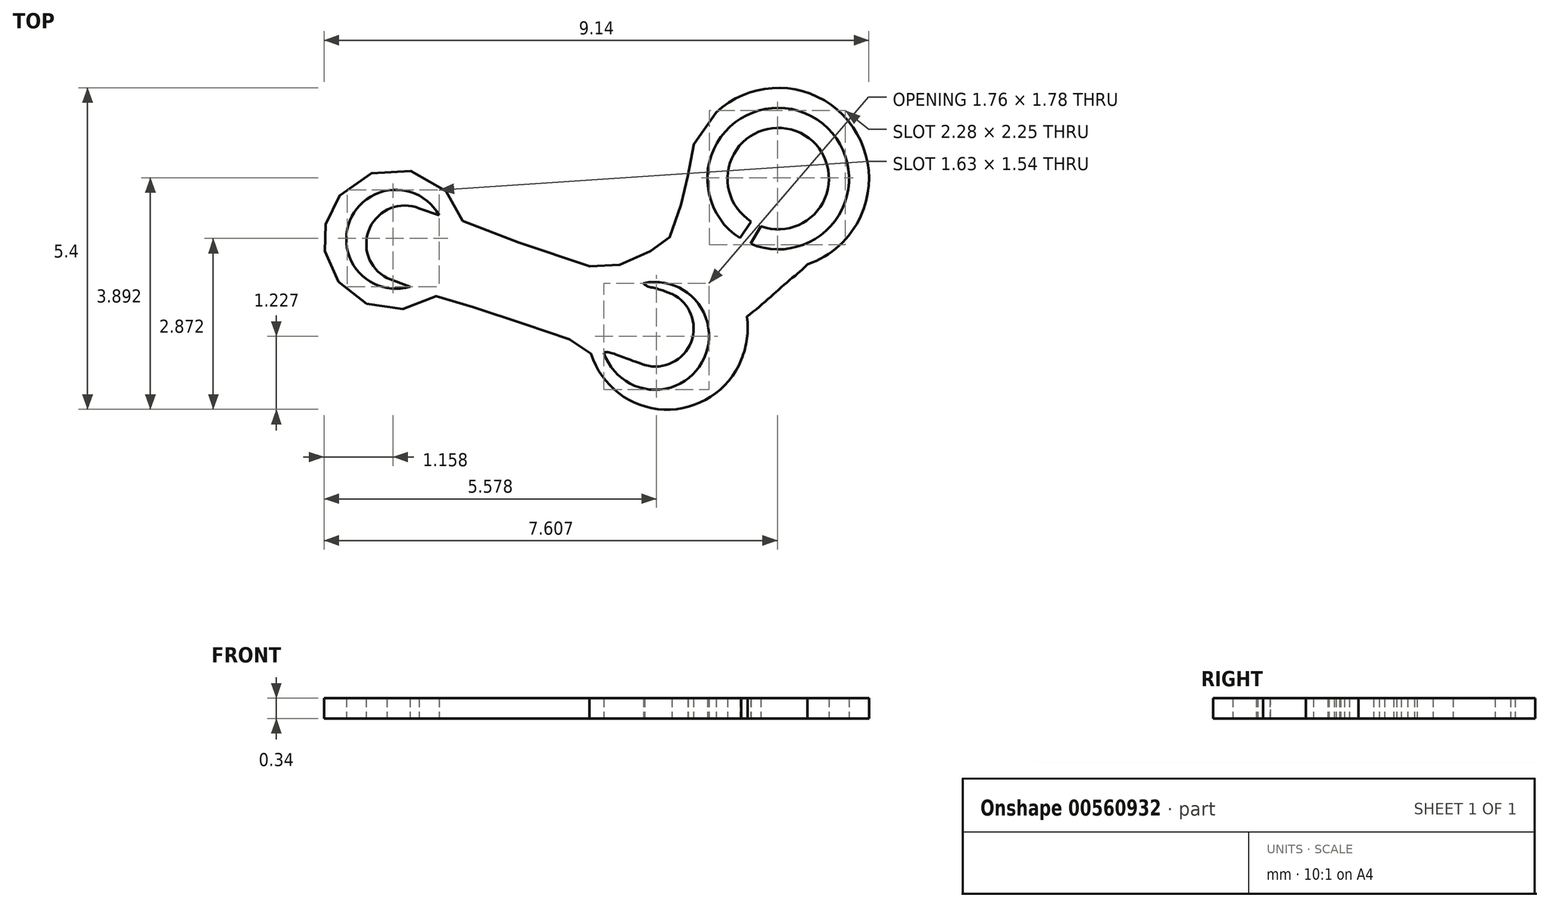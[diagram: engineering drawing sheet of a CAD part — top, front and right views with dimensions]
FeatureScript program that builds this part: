
annotation { "Feature Type Name" : "Feature", "Feature Type Description" : "" }
export const myFeature = defineFeature(function(context is Context, id is Id, definition is map)
    precondition{}
    {
        {
            var Q0;
            Q0=qCreatedBy(makeId("Top.planeOp"),FACE);
            var sketch = newSketch(context, id + "F0", { "sketchPlane" : qUnion([Q0])});
            skArc(sketch, "E0", {"start": v(13.44, 5.28) * mm, "mid": v(12.94, 7.14) * mm, "end": v(11, 7.02) * mm});
            skFitSpline(sketch, "E1", {"points": [v(11, 7.02) * mm, v(10.83, 6.82) * mm, v(10.71, 6.65) * mm, v(10.6, 6.4) * mm, v(10.58, 6.28) * mm, v(10.54, 6.07) * mm, v(10.54, 5.92) * mm, v(10.54, 5.84) * mm, v(10.5, 5.74) * mm, v(10.44, 5.54) * mm, v(10.37, 5.34) * mm, v(10.32, 5.17) * mm, v(10.25, 4.99) * mm, v(10.2, 4.78) * mm, v(10.17, 4.72) * mm, v(10.08, 4.7) * mm, v(9.9, 4.68) * mm, v(9.75, 4.64) * mm, v(9.6, 4.58) * mm, v(9.4, 4.47) * mm, v(9.24, 4.31) * mm, v(9.23, 4.31) * mm, v(9.1, 4.36) * mm, v(8.75, 4.48) * mm, v(7.82, 4.8) * mm, v(6.78, 5.14) * mm, v(6.78, 5.14) * mm, v(6.76, 5.18) * mm, v(6.73, 5.3) * mm, v(6.66, 5.44) * mm, v(6.52, 5.65) * mm, v(6.34, 5.82) * mm, v(6.1, 5.96) * mm, v(5.8, 6.04) * mm, v(5.55, 6.05) * mm, v(5.31, 6.03) * mm, v(5.02, 5.9) * mm, v(4.83, 5.76) * mm, v(4.68, 5.6) * mm, v(4.58, 5.45) * mm, v(4.52, 5.3) * mm, v(4.46, 5.15) * mm, v(4.44, 5.02) * mm, v(4.43, 4.9) * mm, v(4.43, 4.8) * mm, v(4.45, 4.67) * mm, v(4.5, 4.5) * mm, v(4.56, 4.35) * mm, v(4.69, 4.15) * mm, v(4.83, 4) * mm, v(4.97, 3.9) * mm, v(5.2, 3.78) * mm, v(5.42, 3.72) * mm, v(5.65, 3.71) * mm, v(5.87, 3.73) * mm, v(6.14, 3.83) * mm, v(6.27, 3.9) * mm, v(6.34, 3.95) * mm, v(6.35, 3.95) * mm, v(6.6, 3.86) * mm, v(7.02, 3.72) * mm, v(7.47, 3.57) * mm, v(7.94, 3.42) * mm, v(8.28, 3.3) * mm, v(8.58, 3.2) * mm, v(8.8, 3.13) * mm, v(8.88, 3.1) * mm, v(8.88, 3.09) * mm, v(8.91, 2.97) * mm], "startDerivative": vector(-11.42, -11.44) * mm, "endDerivative": vector(4.05, -13.15) * mm});
            skArc(sketch, "E2", {"start": v(8.91, 2.97) * mm, "mid": v(10.14, 2.03) * mm, "end": v(11.43, 2.87) * mm});
            skArc(sketch, "E3", {"start": v(11.43, 2.87) * mm, "mid": v(11.53, 3.22) * mm, "end": v(11.53, 3.59) * mm});
            skFitSpline(sketch, "E4", {"points": [v(11.53, 3.59) * mm, v(11.86, 3.86) * mm, v(12.13, 4.1) * mm, v(12.4, 4.33) * mm, v(12.54, 4.47) * mm], "startDerivative": vector(1.2, 0.97) * mm, "endDerivative": vector(0.68, 0.67) * mm});
            skArc(sketch, "E5", {"start": v(12.54, 4.47) * mm, "mid": v(13.07, 4.78) * mm, "end": v(13.44, 5.28) * mm});
            skArc(sketch, "E6", {"start": v(9.13, 2.98) * mm, "mid": v(10.77, 2.82) * mm, "end": v(9.8, 4.15) * mm});
            skArc(sketch, "E7", {"start": v(9.81, 2.78) * mm, "mid": v(10.59, 3.16) * mm, "end": v(10.27, 3.97) * mm});
            skFitSpline(sketch, "E8", {"points": [v(10.27, 3.97) * mm, v(10.02, 4.05) * mm, v(9.84, 4.1) * mm, v(9.8, 4.15) * mm], "startDerivative": vector(-0.57, 0.22) * mm, "endDerivative": vector(-0.17, 0.2) * mm});
            skFitSpline(sketch, "E9", {"points": [v(9.81, 2.78) * mm, v(9.37, 2.94) * mm, v(9.18, 3) * mm, v(9.13, 2.98) * mm], "startDerivative": vector(-0.94, 0.33) * mm, "endDerivative": vector(-0.25, -0.12) * mm});
            skArc(sketch, "E10", {"start": v(11.76, 5.1) * mm, "mid": v(12.42, 6.67) * mm, "end": v(11.6, 5.19) * mm});
            skArc(sketch, "E11", {"start": v(6.36, 5.3) * mm, "mid": v(4.86, 5.2) * mm, "end": v(5.87, 4.1) * mm});
            skArc(sketch, "E12", {"start": v(6.03, 5.4) * mm, "mid": v(5.2, 5.08) * mm, "end": v(5.49, 4.23) * mm});
            skFitSpline(sketch, "E13", {"points": [v(6.03, 5.4) * mm, v(6.36, 5.3) * mm], "startDerivative": vector(0.33, -0.11) * mm, "endDerivative": vector(0.33, -0.11) * mm});
            skFitSpline(sketch, "E14", {"points": [v(5.49, 4.23) * mm, v(5.87, 4.1) * mm], "startDerivative": vector(0.39, -0.14) * mm, "endDerivative": vector(0.39, -0.14) * mm});
            skArc(sketch, "E15", {"start": v(11.59, 4.81) * mm, "mid": v(12.6, 6.96) * mm, "end": v(11.4, 4.9) * mm});
            skLineSegment(sketch, "E16", {"start": v(11.6, 5.19) * mm, "end": v(11.4, 4.9) * mm});
            skLineSegment(sketch, "E17", {"start": v(11.76, 5.1) * mm, "end": v(11.59, 4.81) * mm});
            skSolve(sketch);
        }
        {
            var Q0;
            Q0=makeQuery(id+"F0.imprint","IMPRINT",FACE,{"disambiguationData":[TD([[makeQuery(id+"F0.imprint","IMPRINT",EDGE,{"derivedFrom":sQuery(id+"F0.wireOp",EDGE,"E0")}),1.0]])]});
            var Q1;
            Q1=makeQuery(id+"F0.imprint","IMPRINT",FACE,{"disambiguationData":[TD([[makeQuery(id+"F0.imprint","IMPRINT",EDGE,{"derivedFrom":sQuery(id+"F0.wireOp",EDGE,"E10")}),1.0]])]});
            extrude(context, id + "F1", {"entities" : qUnion([Q0, Q1]), "depth" : 0.34 * mm, "offsetDistance" : 25 * mm});
        }
    });
